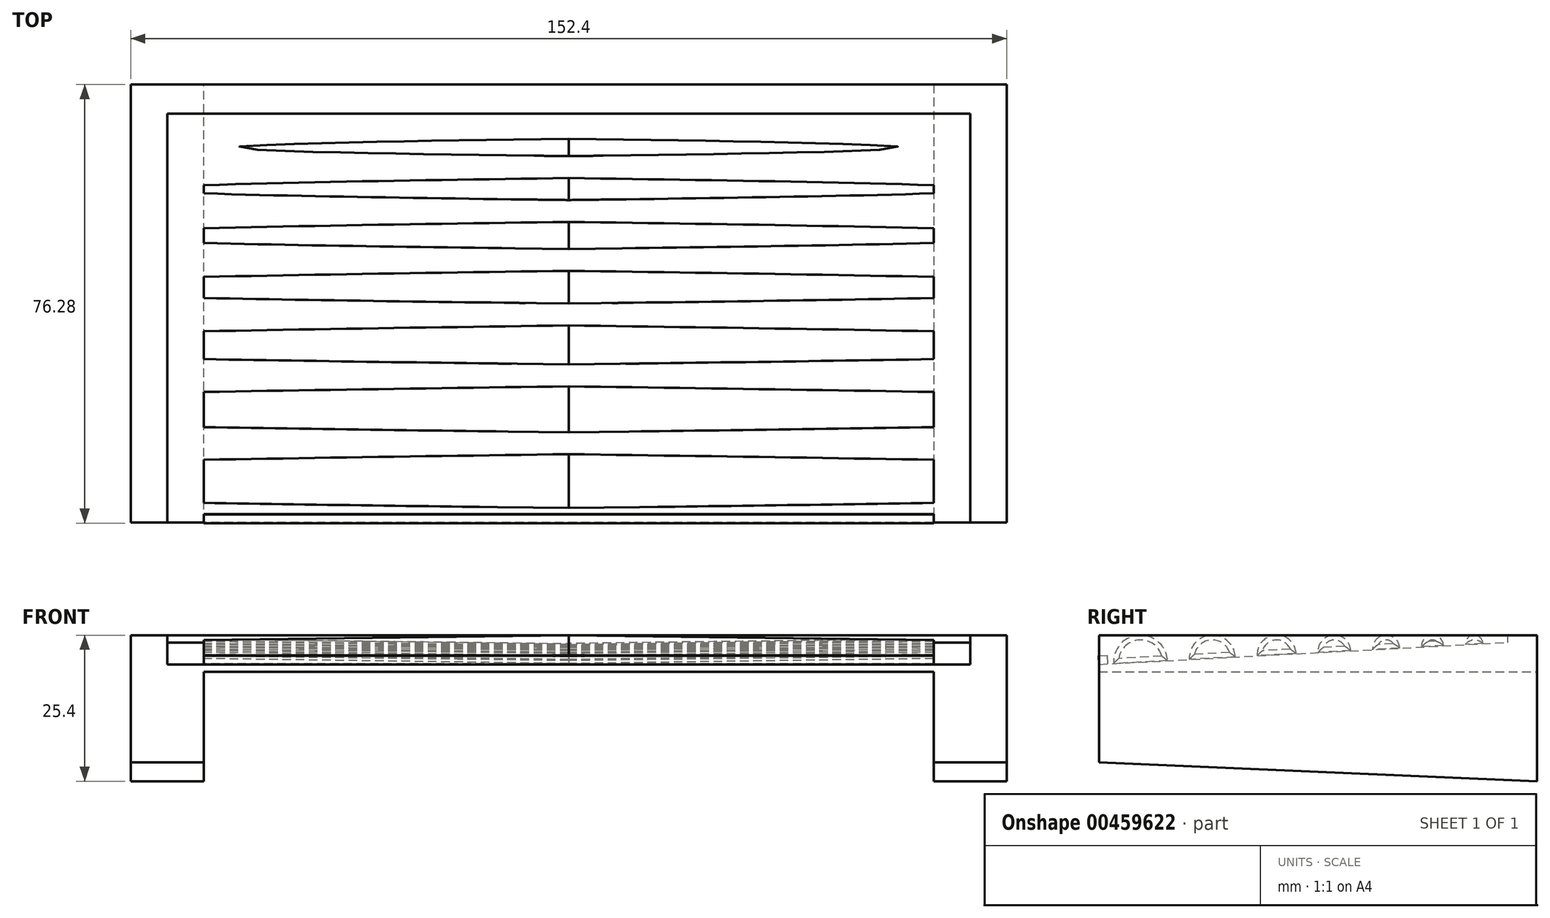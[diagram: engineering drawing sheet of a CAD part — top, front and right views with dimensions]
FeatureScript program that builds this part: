
annotation { "Feature Type Name" : "Feature", "Feature Type Description" : "" }
export const myFeature = defineFeature(function(context is Context, id is Id, definition is map)
    precondition{}
    {
        {
            var Q0;
            Q0=qCreatedBy(makeId("Front.planeOp"),FACE);
            var sketch = newSketch(context, id + "F0", { "sketchPlane" : qUnion([Q0])});
            skLineSegment(sketch, "E0", {"start": v(-76.2, 0) * mm, "end": v(-76.2, 25.4) * mm});
            skLineSegment(sketch, "E1", {"start": v(-76.2, 25.4) * mm, "end": v(76.2, 25.4) * mm});
            skLineSegment(sketch, "E2", {"start": v(76.2, 25.4) * mm, "end": v(76.2, 0) * mm});
            skLineSegment(sketch, "E3", {"start": v(76.2, 0) * mm, "end": v(63.5, 0) * mm});
            skLineSegment(sketch, "E4", {"start": v(63.5, 0) * mm, "end": v(63.5, 19.05) * mm});
            skLineSegment(sketch, "E5", {"start": v(63.5, 19.05) * mm, "end": v(-63.5, 19.05) * mm});
            skLineSegment(sketch, "E6", {"start": v(-63.5, 19.05) * mm, "end": v(-63.5, 0) * mm});
            skLineSegment(sketch, "E7", {"start": v(-63.5, 0) * mm, "end": v(-76.2, 0) * mm});
            skPoint(sketch, "E8", {"position": v(0, 25.4) * mm});
            skPoint(sketch, "E9", {"position": v(0, 19.05) * mm});
            skSolve(sketch);
        }
        {
            var Q0;
            Q0=makeQuery(id+"F0.imprint","IMPRINT",FACE,{"disambiguationData":[TD([[makeQuery(id+"F0.imprint","IMPRINT",EDGE,{"derivedFrom":sQuery(id+"F0.wireOp",EDGE,"E0")}),-1.0]])]});
            extrude(context, id + "F1", {"entities" : qUnion([Q0]), "endBound" : BoundingType.SYMMETRIC, "depth" : 76.2 * mm});
        }
        {
            var Q0;
            Q0=qCreatedBy(makeId("Right.planeOp"),FACE);
            var sketch = newSketch(context, id + "F2", { "sketchPlane" : qUnion([Q0])});
            skLineSegment(sketch, "E10", {"start": v(-38.1, 25.4) * mm, "end": v(-38.1, 20.32) * mm});
            skLineSegment(sketch, "E11", {"start": v(-38.1, 20.32) * mm, "end": v(33.02, 24.13) * mm});
            skLineSegment(sketch, "E12", {"start": v(33.02, 24.13) * mm, "end": v(33.02, 25.4) * mm});
            skLineSegment(sketch, "E13", {"start": v(33.02, 25.4) * mm, "end": v(-38.1, 25.4) * mm});
            skSolve(sketch);
        }
        {
            var Q0;
            Q0 = qSketchRegion(id + "F2", true);
            extrude(context, id + "F3", {"entities" : qUnion([Q0]), "operationType" : NewBodyOperationType.REMOVE, "endBound" : BoundingType.SYMMETRIC, "depth" : 139.7 * mm});
        }
        {
            var Q0;
            Q0=qCreatedBy(makeId("Right.planeOp"),FACE);
            var sketch = newSketch(context, id + "F4", { "sketchPlane" : qUnion([Q0])});
            skLineSegment(sketch, "E14", {"start": v(-38.1, 25.4) * mm, "end": v(-38.1, 20.32) * mm, "construction": true});
            skLineSegment(sketch, "E15", {"start": v(-38.1, 20.32) * mm, "end": v(31.75, 24.13) * mm, "construction": true});
            skLineSegment(sketch, "E16", {"start": v(31.75, 24.13) * mm, "end": v(31.75, 25.4) * mm, "construction": true});
            skLineSegment(sketch, "E17", {"start": v(31.75, 25.4) * mm, "end": v(-38.1, 25.4) * mm, "construction": true});
            skArc(sketch, "E18", {"start": v(-26.2, 20.97) * mm, "mid": v(-31.14, 25.4) * mm, "end": v(-35.56, 20.46) * mm});
            skPoint(sketch, "E19", {"position": v(-35.56, 20.46) * mm});
            skPoint(sketch, "E20", {"position": v(-26.2, 20.97) * mm});
            skArc(sketch, "E21", {"start": v(-14.4, 21.61) * mm, "mid": v(-18.61, 25.4) * mm, "end": v(-22.4, 21.18) * mm});
            skArc(sketch, "E22", {"start": v(-3.8, 22.2) * mm, "mid": v(-7.38, 25.4) * mm, "end": v(-10.58, 21.82) * mm});
            skArc(sketch, "E23", {"start": v(5.69, 22.7) * mm, "mid": v(2.7, 25.4) * mm, "end": v(0, 22.4) * mm});
            skArc(sketch, "E24", {"start": v(14.2, 23.17) * mm, "mid": v(11.72, 25.4) * mm, "end": v(9.5, 22.92) * mm});
            skArc(sketch, "E25", {"start": v(21.84, 23.59) * mm, "mid": v(19.82, 25.4) * mm, "end": v(18.01, 23.38) * mm});
            skArc(sketch, "E26", {"start": v(28.68, 23.96) * mm, "mid": v(27.08, 25.4) * mm, "end": v(25.65, 23.8) * mm});
            skLineSegment(sketch, "E27", {"start": v(-35.56, 20.46) * mm, "end": v(-26.2, 20.97) * mm});
            skLineSegment(sketch, "E28", {"start": v(-22.4, 21.18) * mm, "end": v(-14.4, 21.61) * mm});
            skLineSegment(sketch, "E29", {"start": v(-10.58, 21.82) * mm, "end": v(-3.8, 22.2) * mm});
            skLineSegment(sketch, "E30", {"start": v(0, 22.4) * mm, "end": v(5.69, 22.7) * mm});
            skLineSegment(sketch, "E31", {"start": v(9.5, 22.92) * mm, "end": v(14.2, 23.17) * mm});
            skLineSegment(sketch, "E32", {"start": v(18.01, 23.38) * mm, "end": v(21.84, 23.59) * mm});
            skLineSegment(sketch, "E33", {"start": v(25.65, 23.8) * mm, "end": v(28.68, 23.96) * mm});
            skSolve(sketch);
        }
        {
            var Q0;
            Q0 = qSketchRegion(id + "F4", true);
            extrude(context, id + "F5", {"entities" : qUnion([Q0]), "operationType" : NewBodyOperationType.ADD, "endBound" : BoundingType.SYMMETRIC, "depth" : 127 * mm, "hasDraft" : true, "draftAngle" : .75 * degree, "draftPullDirection" : true});
        }
        {
            var Q0;
            Q0=makeQuery(id+"F1.opExtrude","SWEPT_FACE",FACE,{"disambiguationData":[OSD([sQuery(id+"F0.wireOp",EDGE,"E2")])]});
            var sketch = newSketch(context, id + "F6", { "sketchPlane" : qUnion([Q0])});
            skLineSegment(sketch, "E34", {"start": v(-38.1, 0) * mm, "end": v(-38.1, 3.25) * mm});
            skLineSegment(sketch, "E35", {"start": v(-38.1, 3.25) * mm, "end": v(38.1, 0) * mm});
            skLineSegment(sketch, "E36", {"start": v(38.1, 0) * mm, "end": v(-38.1, 0) * mm});
            skSolve(sketch);
        }
        {
            var Q0;
            Q0 = qSketchRegion(id + "F6", true);
            extrude(context, id + "F7", {"entities" : qUnion([Q0]), "operationType" : NewBodyOperationType.REMOVE, "endBound" : BoundingType.THROUGH_ALL, "oppositeDirection" : true, "depth" : 25 * mm});
        }
        {
            var Q0;
            Q0=makeQuery(id+"F3.boolean.opBoolean","COPY",FACE,{"derivedFrom":makeQuery(id+"F3.opExtrude","SWEPT_FACE",FACE,{"disambiguationData":[OSD([sQuery(id+"F2.wireOp",EDGE,"E11")])]})});
            var sketch = newSketch(context, id + "F8", { "sketchPlane" : qUnion([Q0])});
            skLineSegment(sketch, "E37.bottom", {"start": v(63.5, -36.96) * mm, "end": v(-63.5, -36.96) * mm});
            skLineSegment(sketch, "E37.top", {"start": v(63.5, -35.46) * mm, "end": v(-63.5, -35.46) * mm});
            skLineSegment(sketch, "E37.left", {"start": v(63.5, -36.96) * mm, "end": v(63.5, -35.46) * mm});
            skLineSegment(sketch, "E37.right", {"start": v(-63.5, -36.96) * mm, "end": v(-63.5, -35.46) * mm});
            skSolve(sketch);
        }
        {
            var Q0;
            Q0 = qSketchRegion(id + "F8", true);
            extrude(context, id + "F9", {"entities" : qUnion([Q0]), "operationType" : NewBodyOperationType.ADD, "depth" : 1.5 * mm});
        }
    });
